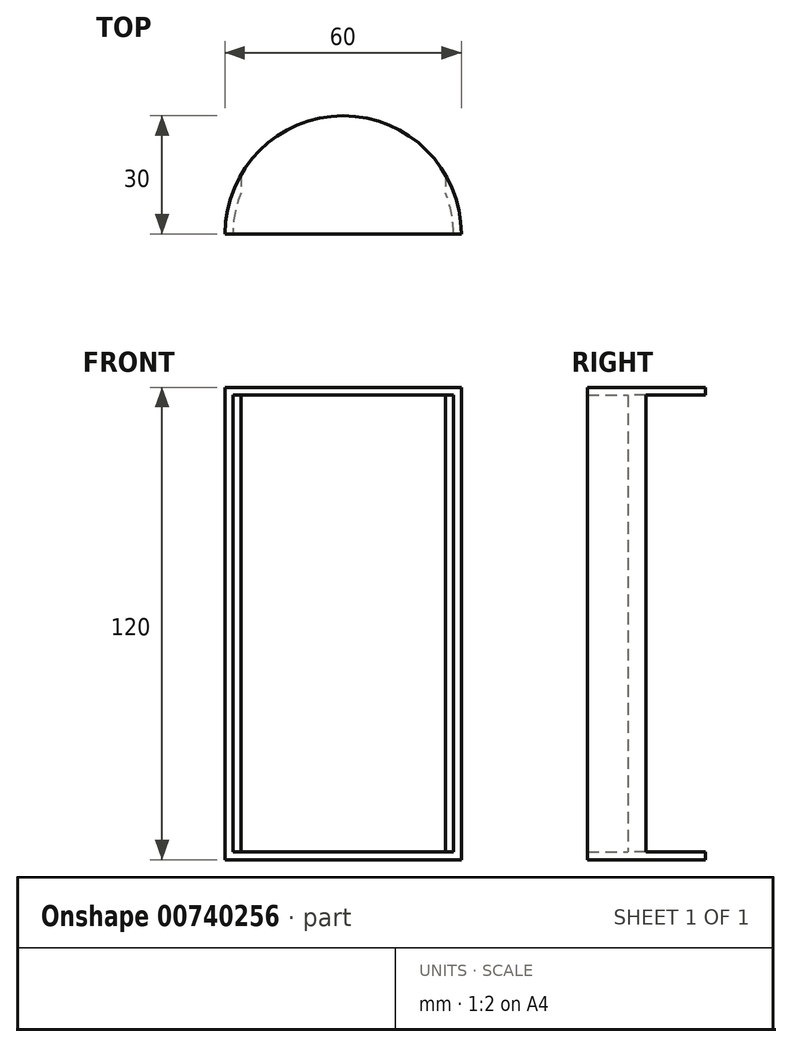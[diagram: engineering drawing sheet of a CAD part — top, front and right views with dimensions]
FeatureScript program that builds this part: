
annotation { "Feature Type Name" : "Feature", "Feature Type Description" : "" }
export const myFeature = defineFeature(function(context is Context, id is Id, definition is map)
    precondition{}
    {
        {
            var Q0;
            Q0=qCreatedBy(makeId("Top.planeOp"),FACE);
            var sketch = newSketch(context, id + "F0", { "sketchPlane" : qUnion([Q0])});
            skArc(sketch, "E0", {"start": v(30, 0) * mm, "mid": v(0, 30) * mm, "end": v(-30, 0) * mm});
            skLineSegment(sketch, "E1", {"start": v(-30, 0) * mm, "end": v(30, 0) * mm});
            skSolve(sketch);
        }
        {
            var Q0;
            Q0 = qSketchRegion(id + "F0", true);
            extrude(context, id + "F1", {"entities" : qUnion([Q0]), "depth" : 120 * mm, "offsetDistance" : 25 * mm, "symmetric" : true});
        }
        {
            var Q0;
            Q0=makeQuery(id+"F1.opExtrude","SWEPT_FACE",FACE,{"disambiguationData":[OSD([sQuery(id+"F0.wireOp",EDGE,"E1")])]});
            shell(context, id + "F2", {"entities" : qUnion([Q0]), "thickness" : 2 * mm});
        }
        {
            var Q0;
            Q0=qCreatedBy(makeId("Front.planeOp"),FACE);
            var sketch = newSketch(context, id + "F3", { "sketchPlane" : qUnion([Q0])});
            skLineSegment(sketch, "E2.bottom", {"start": v(-26, 58) * mm, "end": v(26, 58) * mm});
            skLineSegment(sketch, "E2.top", {"start": v(-26, -58) * mm, "end": v(26, -58) * mm});
            skLineSegment(sketch, "E2.left", {"start": v(-26, 58) * mm, "end": v(-26, -58) * mm});
            skLineSegment(sketch, "E2.right", {"start": v(26, 58) * mm, "end": v(26, -58) * mm});
            skPoint(sketch, "E2.middle", {"position": v(0, 0) * mm});
            skSolve(sketch);
        }
        {
            var Q0;
            Q0 = qSketchRegion(id + "F3", true);
            extrude(context, id + "F4", {"entities" : qUnion([Q0]), "operationType" : NewBodyOperationType.REMOVE, "oppositeDirection" : true, "depth" : 35 * mm, "offsetDistance" : 25 * mm});
        }
    });
